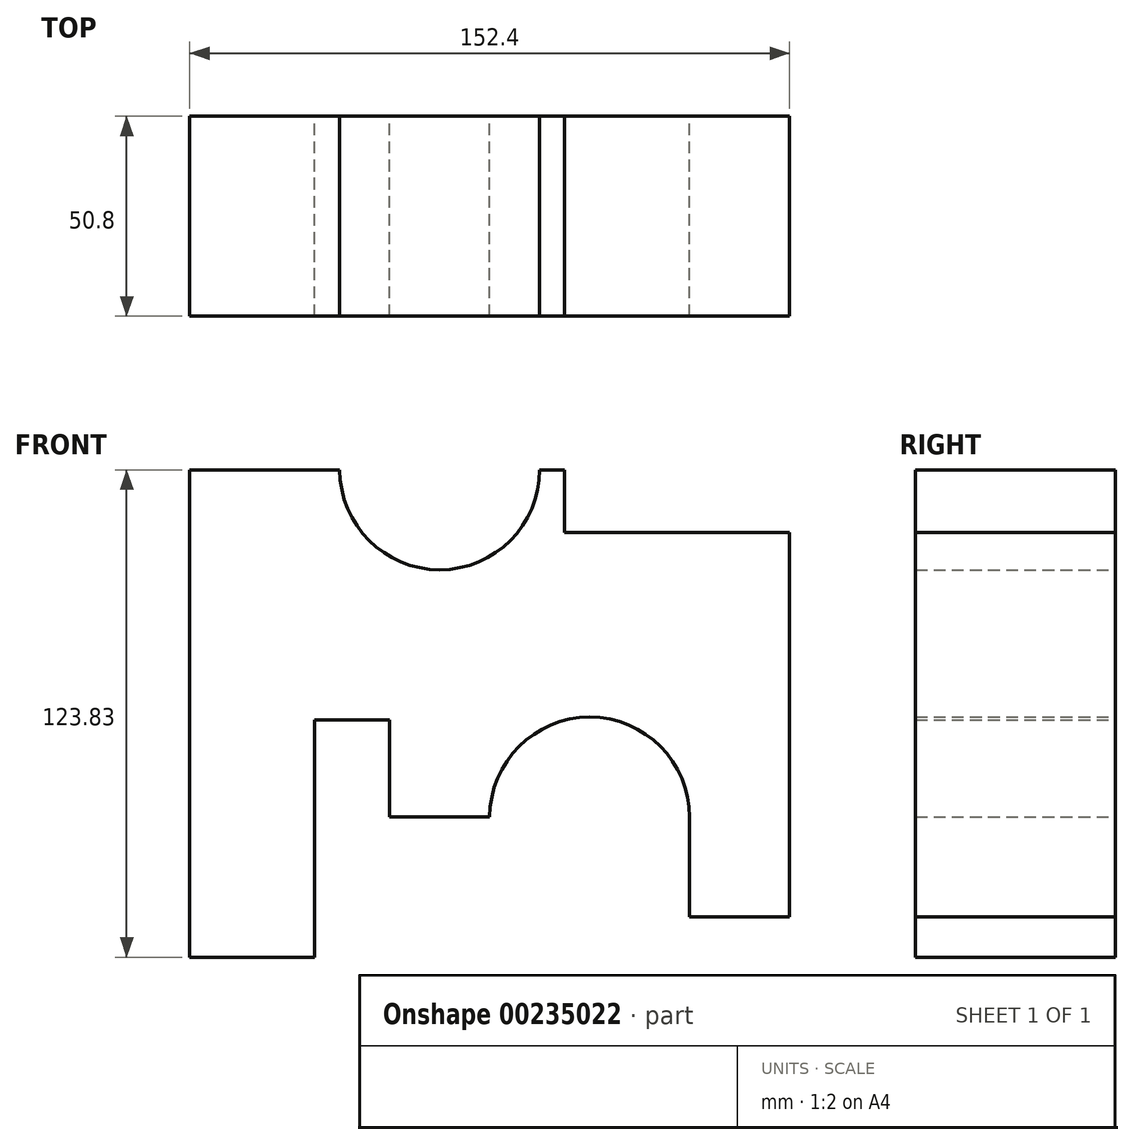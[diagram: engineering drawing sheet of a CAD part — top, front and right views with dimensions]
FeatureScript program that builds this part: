
annotation { "Feature Type Name" : "Feature", "Feature Type Description" : "" }
export const myFeature = defineFeature(function(context is Context, id is Id, definition is map)
    precondition{}
    {
        {
            var Q0;
            Q0=qCreatedBy(makeId("Front.planeOp"),FACE);
            var sketch = newSketch(context, id + "F0", { "sketchPlane" : qUnion([Q0])});
            skLineSegment(sketch, "E0.bottom", {"start": v(0, 0) * mm, "end": v(31.75, 0) * mm});
            skLineSegment(sketch, "E0.left", {"start": v(0, 0) * mm, "end": v(0, 123.83) * mm});
            skLineSegment(sketch, "E0.right", {"start": v(152.4, 10.18) * mm, "end": v(152.4, 107.95) * mm});
            skLineSegment(sketch, "E1", {"start": v(31.75, 0) * mm, "end": v(31.75, 60.33) * mm});
            skLineSegment(sketch, "E2", {"start": v(31.75, 60.33) * mm, "end": v(50.8, 60.33) * mm});
            skLineSegment(sketch, "E3", {"start": v(50.8, 60.33) * mm, "end": v(50.8, 35.58) * mm});
            skLineSegment(sketch, "E4", {"start": v(50.8, 35.58) * mm, "end": v(76.2, 35.58) * mm});
            skLineSegment(sketch, "E5", {"start": v(127, 35.58) * mm, "end": v(127, 10.18) * mm});
            skLineSegment(sketch, "E6", {"start": v(127, 10.18) * mm, "end": v(152.4, 10.18) * mm});
            skArc(sketch, "E7", {"start": v(127, 35.58) * mm, "mid": v(101.6, 60.98) * mm, "end": v(76.2, 35.58) * mm});
            skLineSegment(sketch, "E8", {"start": v(95.25, 123.83) * mm, "end": v(95.25, 107.95) * mm});
            skLineSegment(sketch, "E9", {"start": v(95.25, 107.95) * mm, "end": v(152.4, 107.95) * mm});
            skLineSegment(sketch, "E10", {"start": v(0, 123.83) * mm, "end": v(95.25, 123.83) * mm, "construction": true});
            skArc(sketch, "E11", {"start": v(38.1, 123.83) * mm, "mid": v(63.5, 98.43) * mm, "end": v(88.9, 123.83) * mm});
            skLineSegment(sketch, "E12", {"start": v(38.1, 123.83) * mm, "end": v(0, 123.83) * mm});
            skLineSegment(sketch, "E13", {"start": v(88.9, 123.83) * mm, "end": v(95.25, 123.83) * mm});
            skLineSegment(sketch, "E14", {"start": v(76.2, 35.58) * mm, "end": v(127, 35.58) * mm, "construction": true});
            skSolve(sketch);
        }
        {
            var Q0;
            Q0 = qSketchRegion(id + "F0", true);
            extrude(context, id + "F1", {"entities" : qUnion([Q0]), "depth" : 50.8 * mm});
        }
    });
